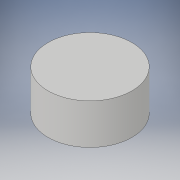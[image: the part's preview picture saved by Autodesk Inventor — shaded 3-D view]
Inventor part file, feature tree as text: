
AUTODESK INVENTOR PART (.ipt)
format: ipt  version: 2019 (Build 230136000, 136)  size: 212,992 bytes
history: native  units: mm
features: extrude x1, sketch x1
ambient origin geometry x8: Origin, YZ Plane, XZ Plane, XY Plane, X Axis, Y Axis, Z Axis, Center Point
bodies: Solid1 (feature_tree)
feature tree (2):
  extrude  "Extrusion1"  Depth=2.6mm TaperAngle=0.0deg
  sketch  "Sketch1"  dims[d0=5.4mm d1=2.6mm d2=0.0mm]
